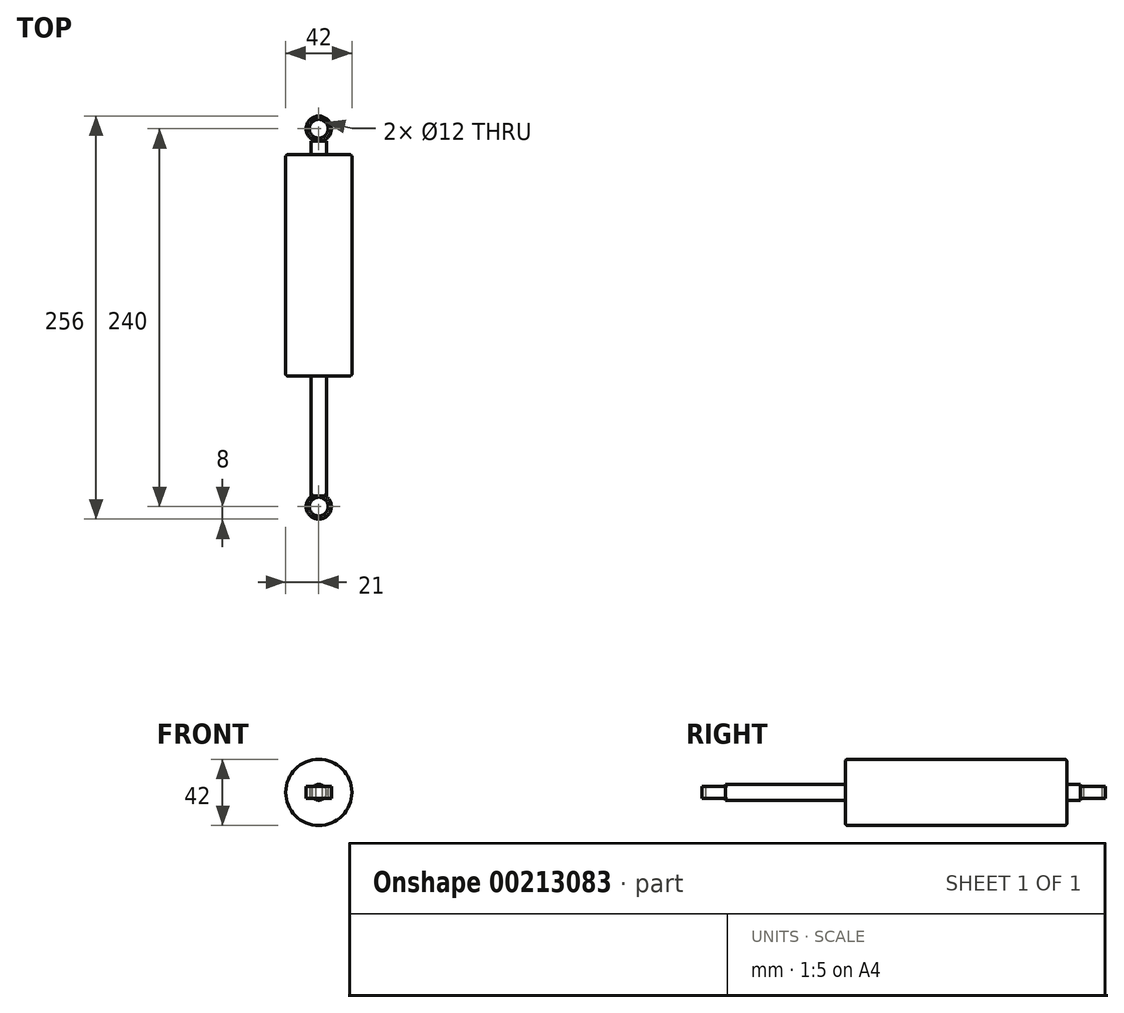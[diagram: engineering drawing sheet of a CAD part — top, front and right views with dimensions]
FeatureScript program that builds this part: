
annotation { "Feature Type Name" : "Feature", "Feature Type Description" : "" }
export const myFeature = defineFeature(function(context is Context, id is Id, definition is map)
    precondition{}
    {
        {
            var Q0;
            Q0=qCreatedBy(makeId("Front.planeOp"),FACE);
            var sketch = newSketch(context, id + "F0", { "sketchPlane" : qUnion([Q0])});
            skCircle(sketch, "E0", {"center": v(0, 0) * mm, "radius": 21 * mm});
            skSolve(sketch);
        }
        {
            var Q0;
            Q0=makeQuery(id+"F0.imprint","IMPRINT",FACE,{"disambiguationData":[TD([[makeQuery(id+"F0.imprint","IMPRINT",EDGE,{"derivedFrom":sQuery(id+"F0.wireOp",EDGE,"E0")}),1.0]])]});
            var Q1;
            Q1=sQuery(id+"F0.wireOp",EDGE,"E0");
            extrude(context, id + "F1", {"entities" : qUnion([Q0]), "surfaceEntities" : qUnion([Q1]), "oppositeDirection" : true, "depth" : 140.5 * mm});
        }
        {
            var Q0;
            Q0=makeQuery(id+"F1.opExtrude","CAP_FACE",FACE,{"disambiguationData":[OSD([sQuery(id+"F0.wireOp",EDGE,"E0")])],"isStart":true});
            var sketch = newSketch(context, id + "F2", { "sketchPlane" : qUnion([Q0])});
            skCircle(sketch, "E1", {"center": v(0, 0) * mm, "radius": 5 * mm});
            skSolve(sketch);
        }
        {
            var Q0;
            Q0 = qSketchRegion(id + "F2", true);
            var Q1;
            Q1 = qSketchRegion(id + "F4", true);
            extrude(context, id + "F3", {"entities" : qUnion([Q0, Q1]), "operationType" : NewBodyOperationType.ADD, "depth" : 75 * mm});
        }
        {
            var Q0;
            Q0=qCreatedBy(makeId("Top.planeOp"),FACE);
            var sketch = newSketch(context, id + "F4", { "sketchPlane" : qUnion([Q0])});
            skLineSegment(sketch, "E2", {"start": v(0, -75) * mm, "end": v(0, -83) * mm, "construction": true});
            skCircle(sketch, "E3", {"center": v(0, -83) * mm, "radius": 8 * mm});
            skCircle(sketch, "E4.0", {"center": v(0, -83) * mm, "radius": 6 * mm});
            skSolve(sketch);
        }
        {
            var Q0;
            Q0=makeQuery(id+"F4.imprint","IMPRINT",FACE,{"disambiguationData":[TD([[makeQuery(id+"F4.imprint","IMPRINT",EDGE,{"derivedFrom":sQuery(id+"F4.wireOp",EDGE,"E3")}),1.0]])]});
            extrude(context, id + "F5", {"entities" : qUnion([Q0]), "operationType" : NewBodyOperationType.ADD, "depth" : 7.5 * mm, "symmetric" : true});
        }
        {
            var Q0;
            Q0=makeQuery(id+"F5.opExtrude","SWEPT_BODY",BODY,{"disambiguationData":[OSD([sQuery(id+"F4.wireOp",EDGE,"E3"),sQuery(id+"F4.wireOp",EDGE,"E4.0")])]});
            transform(context, id + "F6", {"entities" : qUnion([Q0]), "transformType" : TransformType.TRANSLATION_3D, "dx" : 0 * mm, "dy" : 240 * mm, "dz" : 0 * mm, "makeCopy" : true});
        }
        {
            var Q0;
            Q0=makeQuery(id+"F1.opExtrude","CAP_FACE",FACE,{"disambiguationData":[OSD([sQuery(id+"F0.wireOp",EDGE,"E0")])],"isStart":false});
            var sketch = newSketch(context, id + "F7", { "sketchPlane" : qUnion([Q0])});
            skCircle(sketch, "E5", {"center": v(0, 0) * mm, "radius": 5 * mm});
            skSolve(sketch);
        }
        {
            var Q0;
            Q0=makeQuery(id+"F7.imprint","IMPRINT",FACE,{"disambiguationData":[TD([[makeQuery(id+"F7.imprint","IMPRINT",EDGE,{"derivedFrom":sQuery(id+"F7.wireOp",EDGE,"E5")}),1.0]])]});
            var Q1;
            Q1=sQuery(id+"F7.wireOp",EDGE,"E5");
            extrude(context, id + "F8", {"entities" : qUnion([Q0]), "operationType" : NewBodyOperationType.ADD, "surfaceEntities" : qUnion([Q1]), "depth" : 8.8 * mm});
        }
        {
            var Q0;
            Q0=makeQuery(id+"F3.opExtrude","CAP_FACE",FACE,{"disambiguationData":[OSD([sQuery(id+"F2.wireOp",EDGE,"E1")])],"isStart":false});
            extrude(context, id + "F9", {"entities" : qUnion([Q0]), "operationType" : NewBodyOperationType.ADD, "depth" : 1.27 * mm});
        }
        {
            var Q0;
            Q0=makeQuery(id+"F1.opExtrude","CAP_EDGE",EDGE,{"disambiguationData":[OSD([sQuery(id+"F0.wireOp",EDGE,"E0")])],"isStart":true});
            var Q1;
            Q1=makeQuery(id+"F1.opExtrude","CAP_EDGE",EDGE,{"disambiguationData":[OSD([sQuery(id+"F0.wireOp",EDGE,"E0")])],"isStart":false});
            fillet(context, id + "F10", {"entities" : qUnion([Q0, Q1]), "radius" : 1.27 * mm, "tangentPropagation" : true, "allowEdgeOverflow" : false});
        }
        {
            var Q0;
            Q0=makeQuery(id+"F6.opPattern","COPY",EDGE,{"derivedFrom":makeQuery(id+"F5.opExtrude","CAP_EDGE",EDGE,{"disambiguationData":[OSD([sQuery(id+"F4.wireOp",EDGE,"E4.0")])],"isStart":true}),"instanceName":"1"});
            var Q1;
            Q1=makeQuery(id+"F5.opExtrude","CAP_EDGE",EDGE,{"disambiguationData":[OSD([sQuery(id+"F4.wireOp",EDGE,"E4.0")])],"isStart":true});
            var Q2;
            Q2=makeQuery(id+"F3.opExtrude","CAP_EDGE",EDGE,{"disambiguationData":[OSD([sQuery(id+"F2.wireOp",EDGE,"E1")])],"isStart":false});
            var Q3;
            Q3=makeQuery(id+"F5.opExtrude","CAP_EDGE",EDGE,{"disambiguationData":[OSD([sQuery(id+"F4.wireOp",EDGE,"E4.0")])],"isStart":false});
            var Q4;
            Q4=makeQuery(id+"F6.opPattern","COPY",EDGE,{"derivedFrom":makeQuery(id+"F5.opExtrude","CAP_EDGE",EDGE,{"disambiguationData":[OSD([sQuery(id+"F4.wireOp",EDGE,"E4.0")])],"isStart":false}),"instanceName":"1"});
            fillet(context, id + "F11", {"entities" : qUnion([Q0, Q1, Q2, Q3, Q4]), "radius" : .5 * mm, "tangentPropagation" : true, "allowEdgeOverflow" : false});
        }
    });
